AUTODESK INVENTOR PART (.ipt)
format: ipt  version: 2019 (Build 230136000, 136)  size: 137,728 bytes
history: native  units: in
note: dims shown in document units (in); Inventor stores cm internally (conversion verified against a paired STEP export)
features: extrude x2, sketch x2, pattern_linear x1
ambient origin geometry x8: Origin, YZ Plane, XZ Plane, XY Plane, X Axis, Y Axis, Z Axis, Center Point
bodies: Solid1 (feature_tree)
feature tree (5):
  extrude  "Extrusion1"  Depth=3.937in
  pattern_linear  "Rectangular Pattern1"  Count1=50 Spacing1=0.0in
  extrude  "Extrusion2"  Depth=36.2205in TaperAngle=0.0deg
  sketch  "Sketch1"  dims[d0=7.874in d1=3.937in d2=19.685in d3=0.0in]
  sketch  "Sketch2"  dims[d4=3.5433in d6=36.2205in d7=19.685in d8=0.0in]
